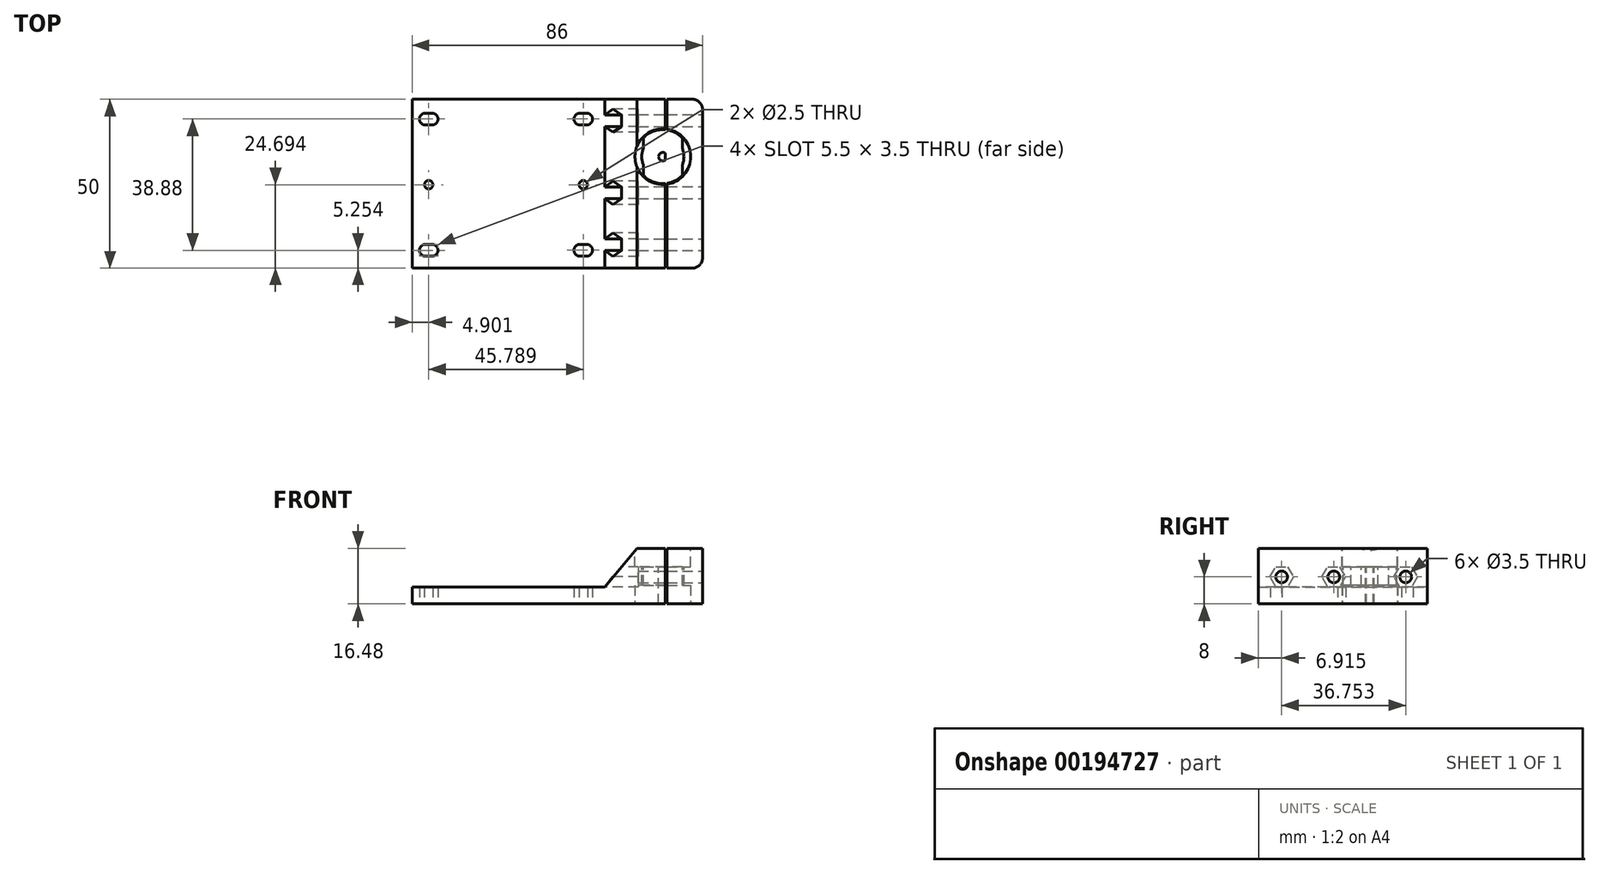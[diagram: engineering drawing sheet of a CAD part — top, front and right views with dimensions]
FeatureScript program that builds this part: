
annotation { "Feature Type Name" : "Feature", "Feature Type Description" : "" }
export const myFeature = defineFeature(function(context is Context, id is Id, definition is map)
    precondition{}
    {
        {
            var Q0;
            Q0=qCreatedBy(makeId("Top.planeOp"),FACE);
            var sketch = newSketch(context, id + "F0", { "sketchPlane" : qUnion([Q0])});
            skLineSegment(sketch, "E0.bottom", {"start": v(0, 0) * mm, "end": v(80, 0) * mm});
            skLineSegment(sketch, "E0.top", {"start": v(0, 50) * mm, "end": v(80, 50) * mm});
            skLineSegment(sketch, "E0.left", {"start": v(0, 0) * mm, "end": v(0, 50) * mm});
            skLineSegment(sketch, "E0.right", {"start": v(80, 0) * mm, "end": v(80, 50) * mm});
            skArc(sketch, "E1", {"start": v(5.9, 42.38) * mm, "mid": v(7.65, 44.13) * mm, "end": v(5.9, 45.88) * mm});
            skArc(sketch, "E2", {"start": v(5.9, 3.5) * mm, "mid": v(7.65, 5.25) * mm, "end": v(5.9, 7) * mm});
            skArc(sketch, "E3", {"start": v(51.68, 3.53) * mm, "mid": v(53.43, 5.28) * mm, "end": v(51.68, 7.03) * mm});
            skArc(sketch, "E4", {"start": v(51.69, 42.38) * mm, "mid": v(53.44, 44.13) * mm, "end": v(51.69, 45.88) * mm});
            skArc(sketch, "E5", {"start": v(3.9, 7) * mm, "mid": v(2.15, 5.25) * mm, "end": v(3.9, 3.5) * mm});
            skLineSegment(sketch, "E6", {"start": v(3.9, 3.5) * mm, "end": v(5.9, 3.5) * mm});
            skLineSegment(sketch, "E7", {"start": v(5.9, 7) * mm, "end": v(3.9, 7) * mm});
            skArc(sketch, "E8", {"start": v(49.68, 7.03) * mm, "mid": v(47.93, 5.28) * mm, "end": v(49.68, 3.53) * mm});
            skLineSegment(sketch, "E9", {"start": v(49.68, 3.53) * mm, "end": v(51.68, 3.53) * mm});
            skLineSegment(sketch, "E10", {"start": v(51.68, 7.03) * mm, "end": v(49.68, 7.03) * mm});
            skArc(sketch, "E11", {"start": v(49.69, 45.88) * mm, "mid": v(47.94, 44.13) * mm, "end": v(49.69, 42.38) * mm});
            skLineSegment(sketch, "E12", {"start": v(49.69, 42.38) * mm, "end": v(51.69, 42.38) * mm});
            skLineSegment(sketch, "E13", {"start": v(49.69, 45.88) * mm, "end": v(51.69, 45.88) * mm});
            skPoint(sketch, "E13.startSnap0", {"position": v(49.69, 46.29) * mm});
            skArc(sketch, "E14", {"start": v(3.9, 45.88) * mm, "mid": v(2.15, 44.13) * mm, "end": v(3.9, 42.38) * mm});
            skLineSegment(sketch, "E15", {"start": v(3.9, 42.38) * mm, "end": v(5.9, 42.38) * mm});
            skLineSegment(sketch, "E16", {"start": v(3.9, 45.88) * mm, "end": v(5.9, 45.88) * mm});
            skPoint(sketch, "E17.endSnap0", {"position": v(53.43, 5.28) * mm});
            skPoint(sketch, "E18", {"position": v(3.9, 5.29) * mm});
            skPoint(sketch, "E19", {"position": v(49.68, 5.29) * mm});
            skSolve(sketch);
        }
        {
            var Q0;
            Q0 = qSketchRegion(id + "F0", true);
            extrude(context, id + "F1", {"entities" : qUnion([Q0]), "depth" : 5 * mm});
        }
        {
            var Q0;
            Q0=makeQuery(id+"F1.opExtrude","CAP_FACE",FACE,{"disambiguationData":[OSD([sQuery(id+"F0.wireOp",EDGE,"E0.bottom"),sQuery(id+"F0.wireOp",EDGE,"E0.top"),sQuery(id+"F0.wireOp",EDGE,"E0.left"),sQuery(id+"F0.wireOp",EDGE,"E0.right"),sQuery(id+"F0.wireOp",EDGE,"E1"),sQuery(id+"F0.wireOp",EDGE,"E2"),sQuery(id+"F0.wireOp",EDGE,"E3"),sQuery(id+"F0.wireOp",EDGE,"E4")])],"isStart":false});
            var sketch = newSketch(context, id + "F2", { "sketchPlane" : qUnion([Q0])});
            skLineSegment(sketch, "E20", {"start": v(57, 0) * mm, "end": v(80, 0) * mm});
            skLineSegment(sketch, "E21", {"start": v(80, 0) * mm, "end": v(80, 50) * mm});
            skLineSegment(sketch, "E22", {"start": v(80, 50) * mm, "end": v(57, 50) * mm});
            skLineSegment(sketch, "E23", {"start": v(57, 50) * mm, "end": v(57, 0) * mm});
            skSolve(sketch);
        }
        {
            var Q0;
            Q0 = qSketchRegion(id + "F2", true);
            extrude(context, id + "F3", {"entities" : qUnion([Q0]), "operationType" : NewBodyOperationType.ADD, "depth" : 15 * mm});
        }
        {
            var Q0;
            Q0=makeQuery(id+"F3.boolean.opBoolean","MERGE",FACE,{"derivedFrom":[makeQuery(id+"F1.opExtrude","SWEPT_FACE",FACE,{"disambiguationData":[OSD([sQuery(id+"F0.wireOp",EDGE,"E0.bottom")])]}),makeQuery(id+"F3.opExtrude","SWEPT_FACE",FACE,{"disambiguationData":[OSD([sQuery(id+"F2.wireOp",EDGE,"E20")])]})]});
            var sketch = newSketch(context, id + "F4", { "sketchPlane" : qUnion([Q0])});
            skLineSegment(sketch, "E24", {"start": v(68.5, 20) * mm, "end": v(57, 5) * mm});
            skLineSegment(sketch, "E25", {"start": v(80, 20) * mm, "end": v(86, 20) * mm});
            skLineSegment(sketch, "E26", {"start": v(86, 20) * mm, "end": v(86, 0) * mm});
            skLineSegment(sketch, "E27", {"start": v(86, 0) * mm, "end": v(80, 0) * mm});
            skSolve(sketch);
        }
        {
            var Q0;
            {var subQ0=sQuery(id+"F4.wireOp",EDGE,"E24");Q0=makeQuery(id+"F4.imprint","IMPRINT",FACE,{"disambiguationData":[TD([[makeQuery(id+"F4.imprint","IMPRINT",EDGE,{"derivedFrom":subQ0}),-1.0]])]});}
            extrude(context, id + "F5", {"entities" : qUnion([Q0]), "operationType" : NewBodyOperationType.REMOVE, "oppositeDirection" : true, "depth" : 50 * mm});
        }
        {
            var Q0;
            Q0=makeQuery(id+"F3.opExtrude","CAP_FACE",FACE,{"disambiguationData":[OSD([sQuery(id+"F2.wireOp",EDGE,"E20"),sQuery(id+"F2.wireOp",EDGE,"E21"),sQuery(id+"F2.wireOp",EDGE,"E22"),sQuery(id+"F2.wireOp",EDGE,"E23")])],"isStart":false});
            var sketch = newSketch(context, id + "F6", { "sketchPlane" : qUnion([Q0])});
            skLineSegment(sketch, "E28", {"start": v(74.25, 50) * mm, "end": v(74.25, 0) * mm});
            skCircle(sketch, "E29", {"center": v(74.25, 33) * mm, "radius": 1.25 * mm});
            skCircle(sketch, "E30", {"center": v(74.25, 33) * mm, "radius": 8 * mm});
            skSolve(sketch);
        }
        {
            var Q0;
            {var subQ0=sQuery(id+"F6.wireOp",EDGE,"E29");var subQ1=sQuery(id+"F6.wireOp",EDGE,"E28");var subQ2=makeQuery(id+"F6.imprint","INTERSECT",VERTEX,{"disambiguationData":[OD(0.0)],"derivedFrom":[subQ1,subQ0]});Q0=makeQuery(id+"F6.imprint","IMPRINT",FACE,{"disambiguationData":[TD([[makeQuery(id+"F6.imprint","IMPRINT",EDGE,{"disambiguationData":[TD([[subQ2,-1.0]])],"derivedFrom":subQ1}),-1.0]])]});}
            var Q1;
            {var subQ0=sQuery(id+"F6.wireOp",EDGE,"E29");var subQ1=sQuery(id+"F6.wireOp",EDGE,"E28");var subQ2=makeQuery(id+"F6.imprint","INTERSECT",VERTEX,{"disambiguationData":[OD(0.0)],"derivedFrom":[subQ1,subQ0]});Q1=makeQuery(id+"F6.imprint","IMPRINT",FACE,{"disambiguationData":[TD([[makeQuery(id+"F6.imprint","IMPRINT",EDGE,{"disambiguationData":[TD([[subQ2,-1.0]])],"derivedFrom":subQ1}),1.0]])]});}
            var Q2;
            Q2=sQuery(id+"F6.wireOp",EDGE,"E29");
            extrude(context, id + "F7", {"entities" : qUnion([Q0, Q1]), "operationType" : NewBodyOperationType.REMOVE, "surfaceEntities" : qUnion([Q2]), "oppositeDirection" : true, "depth" : 25 * mm});
        }
        {
            var Q0;
            Q0=makeQuery(id+"F4.imprint","IMPRINT",FACE,{"disambiguationData":[TD([[makeQuery(id+"F4.imprint","IMPRINT",EDGE,{"derivedFrom":sQuery(id+"F4.wireOp",EDGE,"E25")}),-1.0]])]});
            extrude(context, id + "F8", {"entities" : qUnion([Q0]), "operationType" : NewBodyOperationType.ADD, "oppositeDirection" : true, "depth" : 50 * mm});
        }
        {
            var Q0;
            Q0=makeQuery(id+"F8.boolean.opBoolean","MERGE",FACE,{"derivedFrom":[makeQuery(id+"F3.opExtrude","CAP_FACE",FACE,{"disambiguationData":[OSD([sQuery(id+"F2.wireOp",EDGE,"E20"),sQuery(id+"F2.wireOp",EDGE,"E21"),sQuery(id+"F2.wireOp",EDGE,"E22"),sQuery(id+"F2.wireOp",EDGE,"E23")])],"isStart":false}),makeQuery(id+"F8.opExtrude","SWEPT_FACE",FACE,{"disambiguationData":[OSD([sQuery(id+"F4.wireOp",EDGE,"E25")])]})]});
            var sketch = newSketch(context, id + "F9", { "sketchPlane" : qUnion([Q0])});
            skCircle(sketch, "E31", {"center": v(74.25, 33) * mm, "radius": 8.25 * mm});
            skSolve(sketch);
        }
        {
            var Q0;
            {var subQ0=sQuery(id+"F9.wireOp",EDGE,"E31");var subQ1=makeQuery(id+"F5.boolean.opBoolean","COPY",EDGE,{"derivedFrom":makeQuery(id+"F5.opExtrude","SWEPT_EDGE",EDGE,{"disambiguationData":[OSD([sQuery(id+"F2.wireOp",EDGE,"E20"),sQuery(id+"F4.wireOp",EDGE,"E24")])]})});var subQ2=makeQuery(id+"F9.imprint","INTERSECT",VERTEX,{"disambiguationData":[OD(0.0)],"derivedFrom":[subQ1,subQ0]});Q0=makeQuery(id+"F9.imprint","IMPRINT",FACE,{"disambiguationData":[TD([[makeQuery(id+"F9.imprint","IMPRINT",EDGE,{"disambiguationData":[TD([[subQ2,1.0]])],"derivedFrom":subQ0}),1.0]])]});}
            var Q1;
            Q1=makeQuery(id+"F9.imprint","IMPRINT",FACE,{"disambiguationData":[TD([[makeQuery(id+"F9.imprint","IMPRINT",EDGE,{"derivedFrom":makeQuery(id+"F7.boolean.opBoolean","COPY",EDGE,{"derivedFrom":makeQuery(id+"F7.opExtrude","CAP_EDGE",EDGE,{"disambiguationData":[OSD([sQuery(id+"F6.wireOp",EDGE,"E29")])],"isStart":true})})}),-1.0]])]});
            extrude(context, id + "F10", {"entities" : qUnion([Q0, Q1]), "operationType" : NewBodyOperationType.REMOVE, "oppositeDirection" : true, "depth" : 9 * mm});
        }
        {
            var Q0;
            Q0=makeQuery(id+"F10.boolean.opBoolean","COPY",FACE,{"derivedFrom":makeQuery(id+"F10.opExtrude","CAP_FACE",FACE,{"disambiguationData":[OSD([sQuery(id+"F6.wireOp",EDGE,"E29"),sQuery(id+"F9.wireOp",EDGE,"E31")])],"isStart":false})});
            var sketch = newSketch(context, id + "F11", { "sketchPlane" : qUnion([Q0])});
            skCircle(sketch, "E32", {"center": v(74.25, 33) * mm, "radius": 6.25 * mm});
            skSolve(sketch);
        }
        {
            var Q0;
            Q0=makeQuery(id+"F11.imprint","IMPRINT",FACE,{"disambiguationData":[TD([[makeQuery(id+"F11.imprint","IMPRINT",EDGE,{"derivedFrom":sQuery(id+"F11.wireOp",EDGE,"E32")}),1.0]])]});
            extrude(context, id + "F12", {"entities" : qUnion([Q0]), "operationType" : NewBodyOperationType.REMOVE, "oppositeDirection" : true, "depth" : 6 * mm});
        }
        {
            var Q0;
            Q0=makeQuery(id+"F8.boolean.opBoolean","MERGE",FACE,{"derivedFrom":[makeQuery(id+"F1.opExtrude","CAP_FACE",FACE,{"disambiguationData":[OSD([sQuery(id+"F0.wireOp",EDGE,"E0.bottom"),sQuery(id+"F0.wireOp",EDGE,"E0.top"),sQuery(id+"F0.wireOp",EDGE,"E0.left"),sQuery(id+"F0.wireOp",EDGE,"E0.right"),sQuery(id+"F0.wireOp",EDGE,"E1"),sQuery(id+"F0.wireOp",EDGE,"E2"),sQuery(id+"F0.wireOp",EDGE,"E3"),sQuery(id+"F0.wireOp",EDGE,"E4")])],"isStart":true}),makeQuery(id+"F8.opExtrude","SWEPT_FACE",FACE,{"disambiguationData":[OSD([sQuery(id+"F4.wireOp",EDGE,"E27")])]})]});
            var sketch = newSketch(context, id + "F13", { "sketchPlane" : qUnion([Q0])});
            skCircle(sketch, "E33", {"center": v(74.25, -33) * mm, "radius": 8.25 * mm});
            skSolve(sketch);
        }
        {
            var Q0;
            Q0=makeQuery(id+"F13.imprint","IMPRINT",FACE,{"disambiguationData":[TD([[makeQuery(id+"F13.imprint","IMPRINT",EDGE,{"derivedFrom":sQuery(id+"F13.wireOp",EDGE,"E33")}),1.0]])]});
            extrude(context, id + "F14", {"entities" : qUnion([Q0]), "operationType" : NewBodyOperationType.REMOVE, "oppositeDirection" : true, "depth" : 5.5 * mm});
        }
        {
            var Q0;
            Q0=makeQuery(id+"F8.boolean.opBoolean","MERGE",FACE,{"derivedFrom":[makeQuery(id+"F3.opExtrude","CAP_FACE",FACE,{"disambiguationData":[OSD([sQuery(id+"F2.wireOp",EDGE,"E20"),sQuery(id+"F2.wireOp",EDGE,"E21"),sQuery(id+"F2.wireOp",EDGE,"E22"),sQuery(id+"F2.wireOp",EDGE,"E23")])],"isStart":false}),makeQuery(id+"F8.opExtrude","SWEPT_FACE",FACE,{"disambiguationData":[OSD([sQuery(id+"F4.wireOp",EDGE,"E25")])]})]});
            var sketch = newSketch(context, id + "F15", { "sketchPlane" : qUnion([Q0])});
            skLineSegment(sketch, "E34", {"start": v(75.5, 50) * mm, "end": v(75.5, 0) * mm});
            skLineSegment(sketch, "E35", {"start": v(75.5, 0) * mm, "end": v(75, 0) * mm});
            skLineSegment(sketch, "E36", {"start": v(75, 0) * mm, "end": v(75, 50) * mm});
            skLineSegment(sketch, "E37", {"start": v(75, 50) * mm, "end": v(75.5, 50) * mm});
            skSolve(sketch);
        }
        {
            var Q0;
            {var subQ0=sQuery(id+"F15.wireOp",EDGE,"E37");Q0=makeQuery(id+"F15.imprint","IMPRINT",FACE,{"disambiguationData":[TD([[makeQuery(id+"F15.imprint","IMPRINT",EDGE,{"derivedFrom":subQ0}),-1.0]])]});}
            var Q1;
            {var subQ0=sQuery(id+"F15.wireOp",EDGE,"E34");var subQ1=makeQuery(id+"F10.boolean.opBoolean","COPY",EDGE,{"derivedFrom":makeQuery(id+"F10.opExtrude","CAP_EDGE",EDGE,{"disambiguationData":[OSD([sQuery(id+"F9.wireOp",EDGE,"E31")])],"isStart":true})});var subQ2=makeQuery(id+"F15.imprint","INTERSECT",VERTEX,{"disambiguationData":[OD(0.0)],"derivedFrom":[subQ1,subQ0]});Q1=makeQuery(id+"F15.imprint","IMPRINT",FACE,{"disambiguationData":[TD([[makeQuery(id+"F15.imprint","IMPRINT",EDGE,{"disambiguationData":[TD([[subQ2,-1.0]])],"derivedFrom":subQ0}),-1.0]])]});}
            var Q2;
            {var subQ0=sQuery(id+"F15.wireOp",EDGE,"E35");Q2=makeQuery(id+"F15.imprint","IMPRINT",FACE,{"disambiguationData":[TD([[makeQuery(id+"F15.imprint","IMPRINT",EDGE,{"derivedFrom":subQ0}),1.0]])]});}
            extrude(context, id + "F16", {"entities" : qUnion([Q0, Q1, Q2]), "operationType" : NewBodyOperationType.REMOVE, "oppositeDirection" : true, "depth" : 25 * mm});
        }
        {
            var Q0;
            Q0=makeQuery(id+"F8.opExtrude","CAP_EDGE",EDGE,{"disambiguationData":[OSD([sQuery(id+"F4.wireOp",EDGE,"E26")])],"isStart":true});
            var Q1;
            Q1=makeQuery(id+"F8.opExtrude","CAP_EDGE",EDGE,{"disambiguationData":[OSD([sQuery(id+"F4.wireOp",EDGE,"E26")])],"isStart":false});
            fillet(context, id + "F17", {"entities" : qUnion([Q0, Q1]), "radius" : 3 * mm, "tangentPropagation" : true, "allowEdgeOverflow" : false});
        }
        {
            var Q0;
            {var subQ0=sQuery(id+"F0.wireOp",EDGE,"E0.left");var subQ5=sQuery(id+"F0.wireOp",EDGE,"E0.right");var subQ7=sQuery(id+"F0.wireOp",EDGE,"E0.bottom");var subQ8=sQuery(id+"F2.wireOp",EDGE,"E21");var subQ9=sQuery(id+"F2.wireOp",EDGE,"E20");var subQ10=sQuery(id+"F4.wireOp",EDGE,"E27");var subQ11=sQuery(id+"F4.wireOp",EDGE,"E25");Q0=makeQuery(id+"F16.boolean.opBoolean","SPLIT",FACE,{"disambiguationData":[TD([makeQuery(id+"F1.opExtrude","SWEPT_FACE",FACE,{"disambiguationData":[OSD([subQ0])]})])],"derivedFrom":makeQuery(id+"F8.boolean.opBoolean","MERGE",FACE,{"derivedFrom":[makeQuery(id+"F3.boolean.opBoolean","MERGE",FACE,{"derivedFrom":[makeQuery(id+"F1.opExtrude","SWEPT_FACE",FACE,{"disambiguationData":[OSD([subQ7])]}),makeQuery(id+"F3.opExtrude","SWEPT_FACE",FACE,{"disambiguationData":[OSD([subQ9])]})]}),makeQuery(id+"F8.opExtrude","CAP_FACE",FACE,{"disambiguationData":[OSD([subQ7,subQ5,subQ9,subQ8,subQ11,sQuery(id+"F4.wireOp",EDGE,"E26"),subQ10])],"isStart":true})]})});}
            var sketch = newSketch(context, id + "F18", { "sketchPlane" : qUnion([Q0])});
            skLineSegment(sketch, "E38", {"start": v(69.5, 20) * mm, "end": v(57, 5) * mm});
            skLineSegment(sketch, "E39", {"start": v(57, 5) * mm, "end": v(68.5, 20) * mm});
            skLineSegment(sketch, "E40", {"start": v(68.5, 20) * mm, "end": v(69.5, 20) * mm});
            skSolve(sketch);
        }
        {
            var Q0;
            Q0=makeQuery(id+"F18.imprint","IMPRINT",FACE,{"disambiguationData":[TD([[makeQuery(id+"F18.imprint","IMPRINT",EDGE,{"derivedFrom":sQuery(id+"F18.wireOp",EDGE,"E38")}),-1.0]])]});
            extrude(context, id + "F19", {"entities" : qUnion([Q0]), "operationType" : NewBodyOperationType.REMOVE, "oppositeDirection" : true, "depth" : 55 * mm});
        }
        {
            var Q0;
            Q0=makeQuery(id+"F8.opExtrude","SWEPT_FACE",FACE,{"disambiguationData":[OSD([sQuery(id+"F4.wireOp",EDGE,"E26")])]});
            var sketch = newSketch(context, id + "F20", { "sketchPlane" : qUnion([Q0])});
            skCircle(sketch, "E41", {"center": v(6.91, 8) * mm, "radius": 1.75 * mm});
            skCircle(sketch, "E42", {"center": v(22.36, 8) * mm, "radius": 1.75 * mm});
            skCircle(sketch, "E43", {"center": v(43.67, 8) * mm, "radius": 1.75 * mm});
            skLineSegment(sketch, "E44", {"start": v(3, 0) * mm, "end": v(3, 8) * mm});
            skLineSegment(sketch, "E45", {"start": v(3, 8) * mm, "end": v(47, 8) * mm});
            skSolve(sketch);
        }
        {
            var Q0;
            Q0=makeQuery(id+"F20.imprint","IMPRINT",FACE,{"disambiguationData":[TD([[makeQuery(id+"F20.imprint","IMPRINT",EDGE,{"derivedFrom":sQuery(id+"F20.wireOp",EDGE,"E41")}),1.0]])]});
            var Q1;
            Q1=makeQuery(id+"F20.imprint","IMPRINT",FACE,{"disambiguationData":[TD([[makeQuery(id+"F20.imprint","IMPRINT",EDGE,{"derivedFrom":sQuery(id+"F20.wireOp",EDGE,"E42")}),1.0]])]});
            var Q2;
            Q2=makeQuery(id+"F20.imprint","IMPRINT",FACE,{"disambiguationData":[TD([[makeQuery(id+"F20.imprint","IMPRINT",EDGE,{"derivedFrom":sQuery(id+"F20.wireOp",EDGE,"E43")}),1.0]])]});
            extrude(context, id + "F21", {"entities" : qUnion([Q0, Q1, Q2]), "operationType" : NewBodyOperationType.REMOVE, "oppositeDirection" : true, "depth" : 30 * mm});
        }
        {
            var Q0;
            Q0=makeQuery(id+"F8.opExtrude","SWEPT_FACE",FACE,{"disambiguationData":[OSD([sQuery(id+"F4.wireOp",EDGE,"E26")])]});
            cPlane(context, id + "F22", {"entities" : qUnion([Q0]), "cplaneType" : CPlaneType.OFFSET, "offset" : 29 * mm, "oppositeDirection" : true, "width" : 150 * mm, "height" : 150 * mm});
        }
        {
            var Q0;
            Q0=qCreatedBy(id+"F22.planeOp",FACE);
            var sketch = newSketch(context, id + "F23", { "sketchPlane" : qUnion([Q0])});
            skLineSegment(sketch, "E46", {"start": v(50.16, 0) * mm, "end": v(53.76, 0) * mm});
            skLineSegment(sketch, "E47", {"start": v(53.76, 0) * mm, "end": v(53.76, 8) * mm});
            skLineSegment(sketch, "E48", {"start": v(53.76, 8) * mm, "end": v(47.13, 8) * mm});
            skPoint(sketch, "E49.0.midPoint", {"position": v(47.16, 8) * mm});
            skPoint(sketch, "E50.0.midPoint", {"position": v(25.8, 8) * mm});
            skPoint(sketch, "E51.0.midPoint", {"position": v(10.37, 8) * mm});
            skLineSegment(sketch, "E52.0", {"start": v(41.93, 11) * mm, "end": v(45.4, 11) * mm});
            skLineSegment(sketch, "E52.1", {"start": v(45.4, 11) * mm, "end": v(47.13, 8) * mm});
            skLineSegment(sketch, "E52.2", {"start": v(47.13, 8) * mm, "end": v(45.4, 5) * mm});
            skLineSegment(sketch, "E52.3", {"start": v(45.4, 5) * mm, "end": v(41.93, 5) * mm});
            skLineSegment(sketch, "E52.4", {"start": v(41.93, 5) * mm, "end": v(40.2, 8) * mm});
            skLineSegment(sketch, "E52.5", {"start": v(40.2, 8) * mm, "end": v(41.93, 11) * mm});
            skPoint(sketch, "E52.0.midPoint", {"position": v(43.66, 11) * mm});
            skLineSegment(sketch, "E53.0", {"start": v(20.56, 11) * mm, "end": v(24.02, 11) * mm});
            skLineSegment(sketch, "E53.1", {"start": v(24.02, 11) * mm, "end": v(25.75, 8) * mm});
            skLineSegment(sketch, "E53.2", {"start": v(25.75, 8) * mm, "end": v(24.02, 5) * mm});
            skLineSegment(sketch, "E53.3", {"start": v(24.02, 5) * mm, "end": v(20.56, 5) * mm});
            skLineSegment(sketch, "E53.4", {"start": v(20.56, 5) * mm, "end": v(18.83, 8) * mm});
            skLineSegment(sketch, "E53.5", {"start": v(18.83, 8) * mm, "end": v(20.56, 11) * mm});
            skPoint(sketch, "E53.0.midPoint", {"position": v(22.3, 11) * mm});
            skLineSegment(sketch, "E54.0", {"start": v(5.17, 11) * mm, "end": v(8.64, 11) * mm});
            skLineSegment(sketch, "E54.1", {"start": v(8.64, 11) * mm, "end": v(10.37, 8) * mm});
            skLineSegment(sketch, "E54.2", {"start": v(10.37, 8) * mm, "end": v(8.64, 5) * mm});
            skLineSegment(sketch, "E54.3", {"start": v(8.64, 5) * mm, "end": v(5.17, 5) * mm});
            skLineSegment(sketch, "E54.4", {"start": v(5.17, 5) * mm, "end": v(3.44, 8) * mm});
            skLineSegment(sketch, "E54.5", {"start": v(3.44, 8) * mm, "end": v(5.17, 11) * mm});
            skPoint(sketch, "E54.0.midPoint", {"position": v(6.9, 11) * mm});
            skLineSegment(sketch, "E55.trimOffspring", {"start": v(25.8, 8) * mm, "end": v(25.75, 8) * mm});
            skSolve(sketch);
        }
        {
            var Q0;
            {var subQ0=sQuery(id+"F4.wireOp",EDGE,"E27");var subQ5=sQuery(id+"F0.wireOp",EDGE,"E0.right");var subQ6=sQuery(id+"F0.wireOp",EDGE,"E0.bottom");var subQ7=sQuery(id+"F0.wireOp",EDGE,"E10");var subQ8=sQuery(id+"F0.wireOp",EDGE,"E16");var subQ9=sQuery(id+"F0.wireOp",EDGE,"E9");var subQ10=sQuery(id+"F0.wireOp",EDGE,"E15");var subQ11=sQuery(id+"F0.wireOp",EDGE,"E7");var subQ12=sQuery(id+"F0.wireOp",EDGE,"E14");var subQ13=sQuery(id+"F0.wireOp",EDGE,"E12");var subQ14=sQuery(id+"F0.wireOp",EDGE,"E8");var subQ15=sQuery(id+"F0.wireOp",EDGE,"E1");var subQ16=sQuery(id+"F0.wireOp",EDGE,"E0.left");var subQ17=sQuery(id+"F0.wireOp",EDGE,"E0.top");var subQ18=sQuery(id+"F0.wireOp",EDGE,"E5");var subQ19=sQuery(id+"F0.wireOp",EDGE,"E13");var subQ20=sQuery(id+"F0.wireOp",EDGE,"E2");var subQ21=sQuery(id+"F0.wireOp",EDGE,"E3");var subQ22=sQuery(id+"F0.wireOp",EDGE,"E11");var subQ23=sQuery(id+"F0.wireOp",EDGE,"E4");var subQ24=sQuery(id+"F0.wireOp",EDGE,"E6");Q0=makeQuery(id+"F16.boolean.opBoolean","SPLIT",FACE,{"disambiguationData":[TD([makeQuery(id+"F1.opExtrude","SWEPT_FACE",FACE,{"disambiguationData":[OSD([subQ16])]})])],"derivedFrom":makeQuery(id+"F8.boolean.opBoolean","MERGE",FACE,{"derivedFrom":[makeQuery(id+"F1.opExtrude","CAP_FACE",FACE,{"disambiguationData":[OSD([subQ6,subQ17,subQ16,subQ5,subQ15,subQ20,subQ21,subQ23,subQ18,subQ24,subQ11,subQ14,subQ9,subQ7,subQ22,subQ13,subQ19,subQ12,subQ10,subQ8])],"isStart":true}),makeQuery(id+"F8.opExtrude","SWEPT_FACE",FACE,{"disambiguationData":[OSD([subQ0])]})]})});}
            var sketch = newSketch(context, id + "F24", { "sketchPlane" : qUnion([Q0])});
            skCircle(sketch, "E56", {"center": v(4.9, -24.7) * mm, "radius": 1.25 * mm});
            skCircle(sketch, "E57", {"center": v(50.69, -24.7) * mm, "radius": 1.25 * mm});
            skSolve(sketch);
        }
        {
            var Q0;
            Q0=makeQuery(id+"F24.imprint","IMPRINT",FACE,{"disambiguationData":[TD([[makeQuery(id+"F24.imprint","IMPRINT",EDGE,{"derivedFrom":sQuery(id+"F24.wireOp",EDGE,"E56")}),1.0]])]});
            var Q1;
            Q1=makeQuery(id+"F24.imprint","IMPRINT",FACE,{"disambiguationData":[TD([[makeQuery(id+"F24.imprint","IMPRINT",EDGE,{"derivedFrom":sQuery(id+"F24.wireOp",EDGE,"E57")}),1.0]])]});
            extrude(context, id + "F25", {"entities" : qUnion([Q0, Q1]), "operationType" : NewBodyOperationType.REMOVE, "oppositeDirection" : true, "depth" : 10 * mm});
        }
        {
            var Q0;
            Q0=makeQuery(id+"F23.imprint","IMPRINT",FACE,{"disambiguationData":[TD([[makeQuery(id+"F23.imprint","IMPRINT",EDGE,{"derivedFrom":sQuery(id+"F23.wireOp",EDGE,"E52.0")}),-1.0]])]});
            var Q1;
            Q1=makeQuery(id+"F23.imprint","IMPRINT",FACE,{"disambiguationData":[TD([[makeQuery(id+"F23.imprint","IMPRINT",EDGE,{"derivedFrom":sQuery(id+"F23.wireOp",EDGE,"E53.0")}),-1.0]])]});
            var Q2;
            Q2=makeQuery(id+"F23.imprint","IMPRINT",FACE,{"disambiguationData":[TD([[makeQuery(id+"F23.imprint","IMPRINT",EDGE,{"derivedFrom":sQuery(id+"F23.wireOp",EDGE,"E54.0")}),-1.0]])]});
            extrude(context, id + "F26", {"entities" : qUnion([Q0, Q1, Q2]), "operationType" : NewBodyOperationType.REMOVE, "depth" : 10 * mm});
        }
        {
            var Q0;
            Q0=qCreatedBy(id+"F22.planeOp",FACE);
            var sketch = newSketch(context, id + "F27", { "sketchPlane" : qUnion([Q0])});
            skLineSegment(sketch, "E58", {"start": v(50.41, 19.48) * mm, "end": v(50.41, 16.48) * mm});
            skLineSegment(sketch, "E59", {"start": v(50.41, 16.48) * mm, "end": v(-0.83, 16.48) * mm});
            skLineSegment(sketch, "E60", {"start": v(-0.83, 16.48) * mm, "end": v(-0.83, 20.48) * mm});
            skLineSegment(sketch, "E61", {"start": v(-0.83, 20.48) * mm, "end": v(50.41, 20.48) * mm});
            skLineSegment(sketch, "E62", {"start": v(50.41, 20.48) * mm, "end": v(50.41, 19.48) * mm});
            skSolve(sketch);
        }
        {
            var Q0;
            Q0=makeQuery(id+"F27.imprint","IMPRINT",FACE,{"disambiguationData":[TD([[makeQuery(id+"F27.imprint","IMPRINT",EDGE,{"derivedFrom":sQuery(id+"F27.wireOp",EDGE,"E58")}),-1.0]])]});
            extrude(context, id + "F28", {"entities" : qUnion([Q0]), "operationType" : NewBodyOperationType.REMOVE, "depth" : 30 * mm});
        }
    });
